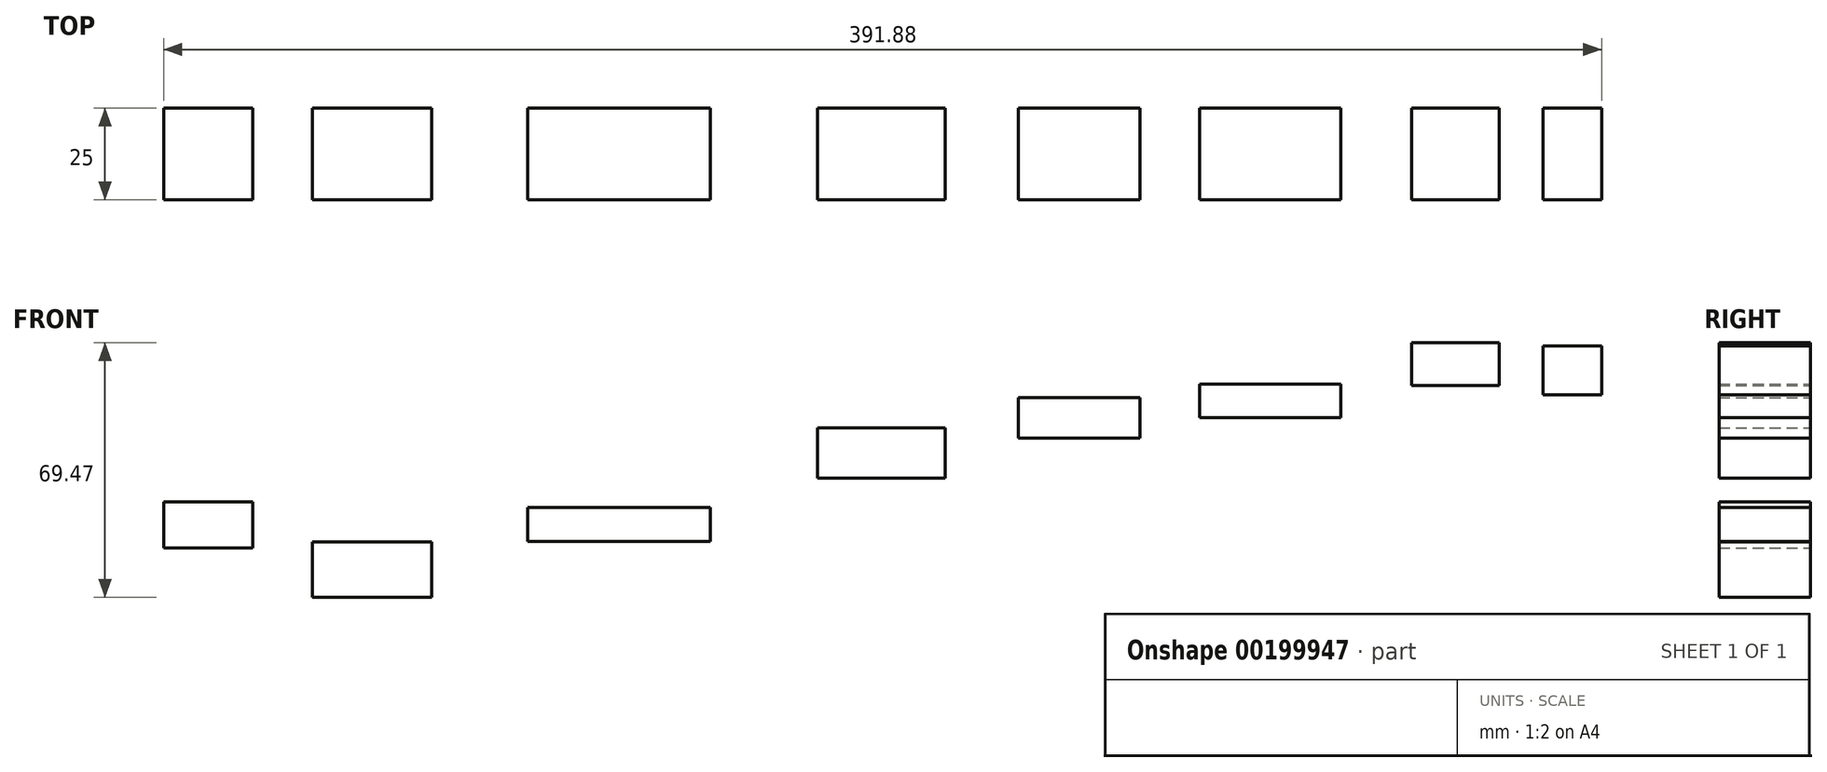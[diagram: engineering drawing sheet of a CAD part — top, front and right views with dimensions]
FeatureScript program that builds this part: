
annotation { "Feature Type Name" : "Feature", "Feature Type Description" : "" }
export const myFeature = defineFeature(function(context is Context, id is Id, definition is map)
    precondition{}
    {
        {
            var Q0;
            Q0=qCreatedBy(makeId("Front.planeOp"),FACE);
            var sketch = newSketch(context, id + "F0", { "sketchPlane" : qUnion([Q0])});
            skLineSegment(sketch, "E0.bottom", {"start": v(-179.18, 70.55) * mm, "end": v(-154.96, 70.55) * mm});
            skLineSegment(sketch, "E0.top", {"start": v(-179.18, 57.97) * mm, "end": v(-154.96, 57.97) * mm});
            skLineSegment(sketch, "E0.left", {"start": v(-179.18, 70.55) * mm, "end": v(-179.18, 57.97) * mm});
            skLineSegment(sketch, "E0.right", {"start": v(-154.96, 70.55) * mm, "end": v(-154.96, 57.97) * mm});
            skLineSegment(sketch, "E1.bottom", {"start": v(-138.7, 59.67) * mm, "end": v(-106.18, 59.67) * mm});
            skLineSegment(sketch, "E1.top", {"start": v(-138.7, 44.5) * mm, "end": v(-106.18, 44.5) * mm});
            skLineSegment(sketch, "E1.left", {"start": v(-138.7, 59.67) * mm, "end": v(-138.7, 44.5) * mm});
            skLineSegment(sketch, "E1.right", {"start": v(-106.18, 59.67) * mm, "end": v(-106.18, 44.5) * mm});
            skLineSegment(sketch, "E2.bottom", {"start": v(-79.97, 69) * mm, "end": v(-30.2, 69) * mm});
            skLineSegment(sketch, "E2.top", {"start": v(-79.97, 59.8) * mm, "end": v(-30.2, 59.8) * mm});
            skLineSegment(sketch, "E2.left", {"start": v(-79.97, 69) * mm, "end": v(-79.97, 59.8) * mm});
            skLineSegment(sketch, "E2.right", {"start": v(-30.2, 69) * mm, "end": v(-30.2, 59.8) * mm});
            skLineSegment(sketch, "E3.bottom", {"start": v(-1, 90.8) * mm, "end": v(33.85, 90.8) * mm});
            skLineSegment(sketch, "E3.top", {"start": v(-1, 76.96) * mm, "end": v(33.85, 76.96) * mm});
            skLineSegment(sketch, "E3.left", {"start": v(-1, 90.8) * mm, "end": v(-1, 76.96) * mm});
            skLineSegment(sketch, "E3.right", {"start": v(33.85, 90.8) * mm, "end": v(33.85, 76.96) * mm});
            skLineSegment(sketch, "E4.bottom", {"start": v(53.76, 98.97) * mm, "end": v(86.94, 98.97) * mm});
            skLineSegment(sketch, "E4.top", {"start": v(53.76, 87.98) * mm, "end": v(86.94, 87.98) * mm});
            skLineSegment(sketch, "E4.left", {"start": v(53.76, 98.97) * mm, "end": v(53.76, 87.98) * mm});
            skLineSegment(sketch, "E4.right", {"start": v(86.94, 98.97) * mm, "end": v(86.94, 87.98) * mm});
            skLineSegment(sketch, "E5.bottom", {"start": v(103.2, 102.63) * mm, "end": v(141.69, 102.63) * mm});
            skLineSegment(sketch, "E5.top", {"start": v(103.2, 93.5) * mm, "end": v(141.69, 93.5) * mm});
            skLineSegment(sketch, "E5.left", {"start": v(103.2, 102.63) * mm, "end": v(103.2, 93.5) * mm});
            skLineSegment(sketch, "E5.right", {"start": v(141.69, 102.63) * mm, "end": v(141.69, 93.5) * mm});
            skLineSegment(sketch, "E6.bottom", {"start": v(160.93, 113.98) * mm, "end": v(184.82, 113.98) * mm});
            skLineSegment(sketch, "E6.top", {"start": v(160.93, 102.3) * mm, "end": v(184.82, 102.3) * mm});
            skLineSegment(sketch, "E6.left", {"start": v(160.93, 113.98) * mm, "end": v(160.93, 102.3) * mm});
            skLineSegment(sketch, "E6.right", {"start": v(184.82, 113.98) * mm, "end": v(184.82, 102.3) * mm});
            skLineSegment(sketch, "E7.bottom", {"start": v(196.77, 113.05) * mm, "end": v(212.7, 113.05) * mm});
            skLineSegment(sketch, "E7.top", {"start": v(196.77, 99.73) * mm, "end": v(212.7, 99.73) * mm});
            skLineSegment(sketch, "E7.left", {"start": v(196.77, 113.05) * mm, "end": v(196.77, 99.73) * mm});
            skLineSegment(sketch, "E7.right", {"start": v(212.7, 113.05) * mm, "end": v(212.7, 99.73) * mm});
            skSolve(sketch);
        }
        {
            var Q0;
            Q0=qSketchRegion(id+"F0",true);
            extrude(context, id + "F1", {"entities" : qUnion([Q0]), "depth" : 25 * mm});
        }
    });
